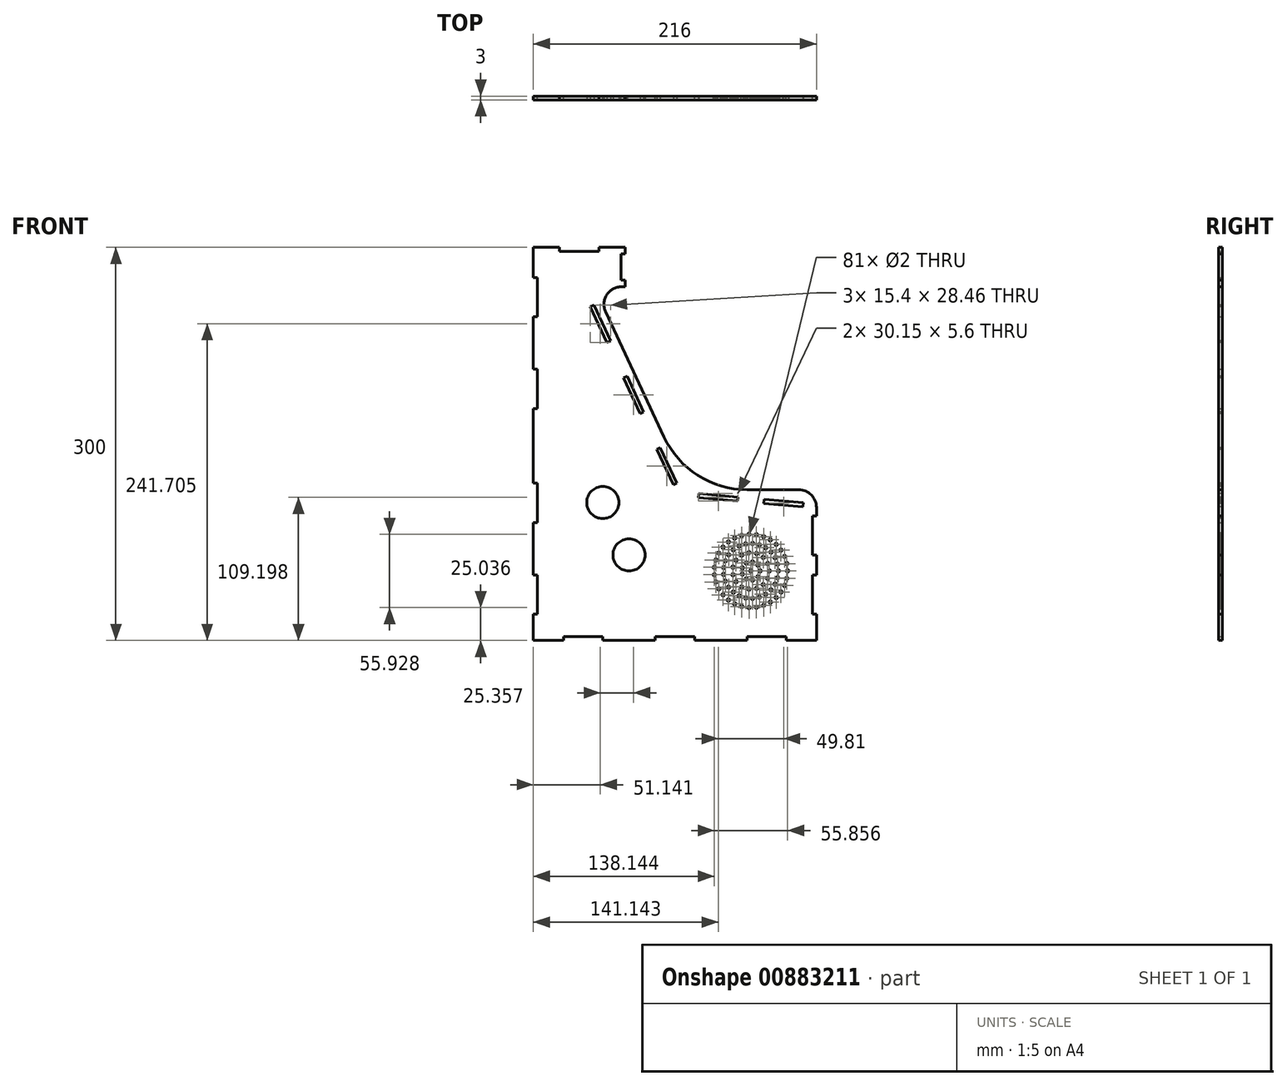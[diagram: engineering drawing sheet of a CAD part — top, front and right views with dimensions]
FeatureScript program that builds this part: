
annotation { "Feature Type Name" : "Feature", "Feature Type Description" : "" }
export const myFeature = defineFeature(function(context is Context, id is Id, definition is map)
    precondition{}
    {
        {
            var Q0;
            Q0=qCreatedBy(makeId("Front.planeOp"),FACE);
            var sketch = newSketch(context, id + "F0", { "sketchPlane" : qUnion([Q0])});
            skLineSegment(sketch, "E0", {"start": v(0, 0) * mm, "end": v(216, 0) * mm});
            skLineSegment(sketch, "E1", {"start": v(216, 0) * mm, "end": v(216, 115) * mm});
            skLineSegment(sketch, "E2", {"start": v(216, 115) * mm, "end": v(118.5, 115) * mm});
            skLineSegment(sketch, "E3", {"start": v(118.5, 115) * mm, "end": v(46.22, 270) * mm});
            skLineSegment(sketch, "E4", {"start": v(46.22, 270) * mm, "end": v(70, 270) * mm});
            skLineSegment(sketch, "E5", {"start": v(70, 270) * mm, "end": v(70, 300) * mm});
            skLineSegment(sketch, "E6", {"start": v(70, 300) * mm, "end": v(0, 300) * mm});
            skLineSegment(sketch, "E7", {"start": v(0, 300) * mm, "end": v(0, 0) * mm});
            skLineSegment(sketch, "E8", {"start": v(0, 277) * mm, "end": v(3, 277) * mm});
            skLineSegment(sketch, "E9", {"start": v(3, 277) * mm, "end": v(3, 247) * mm});
            skLineSegment(sketch, "E10", {"start": v(3, 247) * mm, "end": v(0, 247) * mm});
            skLineSegment(sketch, "E11", {"start": v(0, 207) * mm, "end": v(3, 207) * mm});
            skLineSegment(sketch, "E12", {"start": v(3, 207) * mm, "end": v(3, 177) * mm});
            skLineSegment(sketch, "E13", {"start": v(3, 177) * mm, "end": v(0, 177) * mm});
            skLineSegment(sketch, "E14", {"start": v(0, 120) * mm, "end": v(3, 120) * mm});
            skLineSegment(sketch, "E15", {"start": v(3, 120) * mm, "end": v(3, 90) * mm});
            skLineSegment(sketch, "E16", {"start": v(3, 90) * mm, "end": v(0, 90) * mm});
            skLineSegment(sketch, "E17", {"start": v(0, 50) * mm, "end": v(3, 50) * mm});
            skLineSegment(sketch, "E18", {"start": v(3, 50) * mm, "end": v(3, 20) * mm});
            skLineSegment(sketch, "E19", {"start": v(3, 20) * mm, "end": v(0, 20) * mm});
            skLineSegment(sketch, "E20", {"start": v(23, 0) * mm, "end": v(23, 3) * mm});
            skLineSegment(sketch, "E21", {"start": v(23, 3) * mm, "end": v(53, 3) * mm});
            skLineSegment(sketch, "E22", {"start": v(53, 3) * mm, "end": v(53, 0) * mm});
            skLineSegment(sketch, "E23", {"start": v(93, 0) * mm, "end": v(93, 3) * mm});
            skLineSegment(sketch, "E24", {"start": v(93, 3) * mm, "end": v(123, 3) * mm});
            skLineSegment(sketch, "E25", {"start": v(123, 3) * mm, "end": v(123, 0) * mm});
            skLineSegment(sketch, "E26", {"start": v(163, 0) * mm, "end": v(163, 3) * mm});
            skLineSegment(sketch, "E27", {"start": v(163, 3) * mm, "end": v(193, 3) * mm});
            skLineSegment(sketch, "E28", {"start": v(193, 3) * mm, "end": v(193, 0) * mm});
            skLineSegment(sketch, "E29", {"start": v(216, 20) * mm, "end": v(213, 20) * mm});
            skLineSegment(sketch, "E30", {"start": v(213, 20) * mm, "end": v(213, 50) * mm});
            skLineSegment(sketch, "E31", {"start": v(213, 50) * mm, "end": v(216, 50) * mm});
            skLineSegment(sketch, "E32", {"start": v(216, 65) * mm, "end": v(213, 65) * mm});
            skLineSegment(sketch, "E33", {"start": v(213, 65) * mm, "end": v(213, 95) * mm});
            skLineSegment(sketch, "E34", {"start": v(213, 95) * mm, "end": v(216, 95) * mm});
            skLineSegment(sketch, "E35", {"start": v(20, 300) * mm, "end": v(20, 297) * mm});
            skLineSegment(sketch, "E36", {"start": v(20, 297) * mm, "end": v(50, 297) * mm});
            skLineSegment(sketch, "E37", {"start": v(50, 297) * mm, "end": v(50, 300) * mm});
            skLineSegment(sketch, "E38", {"start": v(70, 295) * mm, "end": v(67, 295) * mm});
            skLineSegment(sketch, "E39", {"start": v(67, 295) * mm, "end": v(67, 275) * mm});
            skLineSegment(sketch, "E40", {"start": v(67, 275) * mm, "end": v(70, 275) * mm});
            skPoint(sketch, "E41", {"position": v(108, 3) * mm});
            skPoint(sketch, "E42", {"position": v(108, 0) * mm});
            skPoint(sketch, "E43", {"position": v(167.25, 115) * mm});
            skSolve(sketch);
        }
        {
            var Q0;
            {var subQ12=sQuery(id+"F0.wireOp",EDGE,"E2");Q0=makeQuery(id+"F0.imprint","IMPRINT",FACE,{"disambiguationData":[TD([[makeQuery(id+"F0.imprint","IMPRINT",EDGE,{"derivedFrom":subQ12}),1.0]])]});}
            var Q1;
            {var subQ0=sQuery(id+"F0.wireOp",EDGE,"E4");Q1=makeQuery(id+"F0.imprint","IMPRINT",FACE,{"disambiguationData":[TD([[makeQuery(id+"F0.imprint","IMPRINT",EDGE,{"derivedFrom":subQ0}),-1.0]])]});}
            var Q2;
            {var subQ3=sQuery(id+"F0.wireOp",EDGE,"8a221613-648f-4b06-892d-30c6be6bba23");Q2=makeQuery(id+"F0.imprint","IMPRINT",FACE,{"disambiguationData":[TD([[makeQuery(id+"F0.imprint","IMPRINT",EDGE,{"derivedFrom":subQ3}),-1.0]])]});}
            var Q3;
            {var subQ3=sQuery(id+"F0.wireOp",EDGE,"1dd4d70c-26e7-4ac6-b2af-ccda843abb65");Q3=makeQuery(id+"F0.imprint","IMPRINT",FACE,{"disambiguationData":[TD([[makeQuery(id+"F0.imprint","IMPRINT",EDGE,{"derivedFrom":subQ3}),1.0]])]});}
            extrude(context, id + "F1", {"entities" : qUnion([Q0, Q1, Q2, Q3]), "depth" : 3 * mm, "offsetDistance" : 25 * mm});
        }
        {
            var Q0;
            Q0=makeQuery(id+"F1.opExtrude","CAP_FACE",FACE,{"disambiguationData":[OSD([sQuery(id+"F0.wireOp",EDGE,"E0"),sQuery(id+"F0.wireOp",EDGE,"E1"),sQuery(id+"F0.wireOp",EDGE,"E2"),sQuery(id+"F0.wireOp",EDGE,"E3"),sQuery(id+"F0.wireOp",EDGE,"E4"),sQuery(id+"F0.wireOp",EDGE,"E5"),sQuery(id+"F0.wireOp",EDGE,"E6"),sQuery(id+"F0.wireOp",EDGE,"E7"),sQuery(id+"F0.wireOp",EDGE,"E8"),sQuery(id+"F0.wireOp",EDGE,"E9"),sQuery(id+"F0.wireOp",EDGE,"E10"),sQuery(id+"F0.wireOp",EDGE,"E11"),sQuery(id+"F0.wireOp",EDGE,"E12"),sQuery(id+"F0.wireOp",EDGE,"E13"),sQuery(id+"F0.wireOp",EDGE,"E14"),sQuery(id+"F0.wireOp",EDGE,"E15"),sQuery(id+"F0.wireOp",EDGE,"E16"),sQuery(id+"F0.wireOp",EDGE,"E17"),sQuery(id+"F0.wireOp",EDGE,"E18"),sQuery(id+"F0.wireOp",EDGE,"E19"),sQuery(id+"F0.wireOp",EDGE,"E20"),sQuery(id+"F0.wireOp",EDGE,"E21"),sQuery(id+"F0.wireOp",EDGE,"E22"),sQuery(id+"F0.wireOp",EDGE,"E23"),sQuery(id+"F0.wireOp",EDGE,"E24"),sQuery(id+"F0.wireOp",EDGE,"E25"),sQuery(id+"F0.wireOp",EDGE,"E26"),sQuery(id+"F0.wireOp",EDGE,"E27"),sQuery(id+"F0.wireOp",EDGE,"E28"),sQuery(id+"F0.wireOp",EDGE,"E29"),sQuery(id+"F0.wireOp",EDGE,"E30"),sQuery(id+"F0.wireOp",EDGE,"E31"),sQuery(id+"F0.wireOp",EDGE,"E32"),sQuery(id+"F0.wireOp",EDGE,"E33"),sQuery(id+"F0.wireOp",EDGE,"E34"),sQuery(id+"F0.wireOp",EDGE,"E35"),sQuery(id+"F0.wireOp",EDGE,"E36"),sQuery(id+"F0.wireOp",EDGE,"E37"),sQuery(id+"F0.wireOp",EDGE,"E38"),sQuery(id+"F0.wireOp",EDGE,"E39"),sQuery(id+"F0.wireOp",EDGE,"E40")])],"isStart":false});
            var sketch = newSketch(context, id + "F2", { "sketchPlane" : qUnion([Q0])});
            skLineSegment(sketch, "E44", {"start": v(0, 354.93) * mm, "end": v(177.98, -26.76) * mm, "construction": true});
            skLineSegment(sketch, "E45", {"start": v(3, 122.8) * mm, "end": v(213, 104.42) * mm, "construction": true});
            skLineSegment(sketch, "E46", {"start": v(126.33, 112) * mm, "end": v(156.22, 109.39) * mm});
            skLineSegment(sketch, "E47", {"start": v(156.22, 109.39) * mm, "end": v(155.96, 106.4) * mm});
            skLineSegment(sketch, "E48", {"start": v(155.96, 106.4) * mm, "end": v(126.07, 109.01) * mm});
            skLineSegment(sketch, "E49", {"start": v(126.07, 109.01) * mm, "end": v(126.33, 112) * mm});
            skLineSegment(sketch, "E50", {"start": v(176.14, 107.64) * mm, "end": v(175.88, 104.65) * mm});
            skLineSegment(sketch, "E51", {"start": v(175.88, 104.65) * mm, "end": v(205.77, 102.04) * mm});
            skLineSegment(sketch, "E52", {"start": v(205.77, 102.04) * mm, "end": v(206.03, 105.03) * mm});
            skLineSegment(sketch, "E53", {"start": v(206.03, 105.03) * mm, "end": v(176.14, 107.64) * mm});
            skLineSegment(sketch, "E54", {"start": v(71.52, 201.56) * mm, "end": v(68.8, 200.29) * mm});
            skLineSegment(sketch, "E55", {"start": v(68.8, 200.29) * mm, "end": v(81.48, 173.1) * mm});
            skLineSegment(sketch, "E56", {"start": v(81.48, 173.1) * mm, "end": v(84.2, 174.37) * mm});
            skLineSegment(sketch, "E57", {"start": v(84.2, 174.37) * mm, "end": v(71.52, 201.56) * mm});
            skLineSegment(sketch, "E58", {"start": v(96.88, 147.18) * mm, "end": v(94.16, 145.9) * mm});
            skLineSegment(sketch, "E59", {"start": v(94.16, 145.9) * mm, "end": v(106.83, 118.72) * mm});
            skLineSegment(sketch, "E60", {"start": v(106.83, 118.72) * mm, "end": v(109.55, 119.99) * mm});
            skLineSegment(sketch, "E61", {"start": v(109.55, 119.99) * mm, "end": v(96.88, 147.18) * mm});
            skPoint(sketch, "E62", {"position": v(112.72, 113.2) * mm});
            skLineSegment(sketch, "E63", {"start": v(58.84, 228.74) * mm, "end": v(46.16, 255.93) * mm});
            skLineSegment(sketch, "E64", {"start": v(46.16, 255.93) * mm, "end": v(43.44, 254.67) * mm});
            skLineSegment(sketch, "E65", {"start": v(43.44, 254.67) * mm, "end": v(56.12, 227.48) * mm});
            skLineSegment(sketch, "E66", {"start": v(56.12, 227.48) * mm, "end": v(58.84, 228.74) * mm});
            skCircle(sketch, "E67", {"center": v(73, 65.25) * mm, "radius": 12.25 * mm});
            skCircle(sketch, "E68", {"center": v(53, 105.25) * mm, "radius": 12.25 * mm});
            skSolve(sketch);
        }
        {
            var Q0;
            Q0 = qSketchRegion(id + "F2", true);
            var Q1;
            Q1=makeQuery(id+"F1.opExtrude","CAP_FACE",FACE,{"disambiguationData":[OSD([sQuery(id+"F0.wireOp",EDGE,"E0"),sQuery(id+"F0.wireOp",EDGE,"E1"),sQuery(id+"F0.wireOp",EDGE,"E2"),sQuery(id+"F0.wireOp",EDGE,"E3"),sQuery(id+"F0.wireOp",EDGE,"E4"),sQuery(id+"F0.wireOp",EDGE,"E5"),sQuery(id+"F0.wireOp",EDGE,"E6"),sQuery(id+"F0.wireOp",EDGE,"E7"),sQuery(id+"F0.wireOp",EDGE,"E8"),sQuery(id+"F0.wireOp",EDGE,"E9"),sQuery(id+"F0.wireOp",EDGE,"E10"),sQuery(id+"F0.wireOp",EDGE,"E11"),sQuery(id+"F0.wireOp",EDGE,"E12"),sQuery(id+"F0.wireOp",EDGE,"E13"),sQuery(id+"F0.wireOp",EDGE,"E14"),sQuery(id+"F0.wireOp",EDGE,"E15"),sQuery(id+"F0.wireOp",EDGE,"E16"),sQuery(id+"F0.wireOp",EDGE,"E17"),sQuery(id+"F0.wireOp",EDGE,"E18"),sQuery(id+"F0.wireOp",EDGE,"E19"),sQuery(id+"F0.wireOp",EDGE,"E20"),sQuery(id+"F0.wireOp",EDGE,"E21"),sQuery(id+"F0.wireOp",EDGE,"E22"),sQuery(id+"F0.wireOp",EDGE,"E23"),sQuery(id+"F0.wireOp",EDGE,"E24"),sQuery(id+"F0.wireOp",EDGE,"E25"),sQuery(id+"F0.wireOp",EDGE,"E26"),sQuery(id+"F0.wireOp",EDGE,"E27"),sQuery(id+"F0.wireOp",EDGE,"E28"),sQuery(id+"F0.wireOp",EDGE,"E29"),sQuery(id+"F0.wireOp",EDGE,"E30"),sQuery(id+"F0.wireOp",EDGE,"E31"),sQuery(id+"F0.wireOp",EDGE,"E32"),sQuery(id+"F0.wireOp",EDGE,"E33"),sQuery(id+"F0.wireOp",EDGE,"E34"),sQuery(id+"F0.wireOp",EDGE,"E35"),sQuery(id+"F0.wireOp",EDGE,"E36"),sQuery(id+"F0.wireOp",EDGE,"E37"),sQuery(id+"F0.wireOp",EDGE,"E38"),sQuery(id+"F0.wireOp",EDGE,"E39"),sQuery(id+"F0.wireOp",EDGE,"E40")])],"isStart":true});
            extrude(context, id + "F3", {"entities" : qUnion([Q0]), "operationType" : NewBodyOperationType.REMOVE, "endBound" : BoundingType.UP_TO_SURFACE, "oppositeDirection" : true, "depth" : 25 * mm, "endBoundEntityFace" : qUnion([Q1]), "offsetDistance" : 25 * mm});
        }
        {
            var Q0;
            Q0=makeQuery(id+"F1.opExtrude","SWEPT_EDGE",EDGE,{"disambiguationData":[OSD([sQuery(id+"F0.wireOp",EDGE,"E1"),sQuery(id+"F0.wireOp",EDGE,"E2")])]});
            var Q1;
            Q1=makeQuery(id+"F1.opExtrude","SWEPT_EDGE",EDGE,{"disambiguationData":[OSD([sQuery(id+"F0.wireOp",EDGE,"E3"),sQuery(id+"F0.wireOp",EDGE,"E4")])]});
            fillet(context, id + "F4", {"entities" : qUnion([Q0, Q1]), "radius" : 13.5 * mm, "tangentPropagation" : true, "allowEdgeOverflow" : false});
        }
        {
            var Q0;
            Q0=makeQuery(id+"F1.opExtrude","SWEPT_EDGE",EDGE,{"disambiguationData":[OSD([sQuery(id+"F0.wireOp",EDGE,"E2"),sQuery(id+"F0.wireOp",EDGE,"E3")])]});
            fillet(context, id + "F5", {"entities" : qUnion([Q0]), "radius" : 70 * mm, "tangentPropagation" : true, "allowEdgeOverflow" : false});
        }
        {
            var Q0;
            Q0=makeQuery(id+"F1.opExtrude","CAP_FACE",FACE,{"disambiguationData":[OSD([sQuery(id+"F0.wireOp",EDGE,"E0"),sQuery(id+"F0.wireOp",EDGE,"E1"),sQuery(id+"F0.wireOp",EDGE,"E2"),sQuery(id+"F0.wireOp",EDGE,"E3"),sQuery(id+"F0.wireOp",EDGE,"E4"),sQuery(id+"F0.wireOp",EDGE,"E5"),sQuery(id+"F0.wireOp",EDGE,"E6"),sQuery(id+"F0.wireOp",EDGE,"E7"),sQuery(id+"F0.wireOp",EDGE,"E8"),sQuery(id+"F0.wireOp",EDGE,"E9"),sQuery(id+"F0.wireOp",EDGE,"E10"),sQuery(id+"F0.wireOp",EDGE,"E11"),sQuery(id+"F0.wireOp",EDGE,"E12"),sQuery(id+"F0.wireOp",EDGE,"E13"),sQuery(id+"F0.wireOp",EDGE,"E14"),sQuery(id+"F0.wireOp",EDGE,"E15"),sQuery(id+"F0.wireOp",EDGE,"E16"),sQuery(id+"F0.wireOp",EDGE,"E17"),sQuery(id+"F0.wireOp",EDGE,"E18"),sQuery(id+"F0.wireOp",EDGE,"E19"),sQuery(id+"F0.wireOp",EDGE,"E20"),sQuery(id+"F0.wireOp",EDGE,"E21"),sQuery(id+"F0.wireOp",EDGE,"E22"),sQuery(id+"F0.wireOp",EDGE,"E23"),sQuery(id+"F0.wireOp",EDGE,"E24"),sQuery(id+"F0.wireOp",EDGE,"E25"),sQuery(id+"F0.wireOp",EDGE,"E26"),sQuery(id+"F0.wireOp",EDGE,"E27"),sQuery(id+"F0.wireOp",EDGE,"E28"),sQuery(id+"F0.wireOp",EDGE,"E29"),sQuery(id+"F0.wireOp",EDGE,"E30"),sQuery(id+"F0.wireOp",EDGE,"E31"),sQuery(id+"F0.wireOp",EDGE,"E32"),sQuery(id+"F0.wireOp",EDGE,"E33"),sQuery(id+"F0.wireOp",EDGE,"E34"),sQuery(id+"F0.wireOp",EDGE,"E35"),sQuery(id+"F0.wireOp",EDGE,"E36"),sQuery(id+"F0.wireOp",EDGE,"E37"),sQuery(id+"F0.wireOp",EDGE,"E38"),sQuery(id+"F0.wireOp",EDGE,"E39"),sQuery(id+"F0.wireOp",EDGE,"E40")])],"isStart":false});
            var sketch = newSketch(context, id + "F6", { "sketchPlane" : qUnion([Q0])});
            skCircle(sketch, "E69", {"center": v(166, 53) * mm, "radius": 1 * mm});
            skCircle(sketch, "E70", {"center": v(173, 53) * mm, "radius": 1 * mm});
            skCircle(sketch, "E71", {"center": v(180, 53) * mm, "radius": 1 * mm});
            skCircle(sketch, "E72", {"center": v(187, 53) * mm, "radius": 1 * mm});
            skCircle(sketch, "E73.1.0", {"center": v(171.36, 57.5) * mm, "radius": 1 * mm});
            skCircle(sketch, "E73.2.0", {"center": v(167.22, 59.9) * mm, "radius": 1 * mm});
            skCircle(sketch, "E73.3.0", {"center": v(162.5, 59.06) * mm, "radius": 1 * mm});
            skCircle(sketch, "E73.4.0", {"center": v(159.42, 55.4) * mm, "radius": 1 * mm});
            skCircle(sketch, "E73.5.0", {"center": v(159.42, 50.6) * mm, "radius": 1 * mm});
            skCircle(sketch, "E73.6.0", {"center": v(162.5, 46.94) * mm, "radius": 1 * mm});
            skCircle(sketch, "E73.7.0", {"center": v(167.22, 46.1) * mm, "radius": 1 * mm});
            skCircle(sketch, "E74.1.0", {"center": v(178.79, 58.7) * mm, "radius": 1 * mm});
            skCircle(sketch, "E74.2.0", {"center": v(175.37, 63.4) * mm, "radius": 1 * mm});
            skCircle(sketch, "E74.3.0", {"center": v(170.33, 66.31) * mm, "radius": 1 * mm});
            skCircle(sketch, "E74.4.0", {"center": v(164.54, 66.92) * mm, "radius": 1 * mm});
            skCircle(sketch, "E74.5.0", {"center": v(159, 65.12) * mm, "radius": 1 * mm});
            skCircle(sketch, "E74.6.0", {"center": v(154.67, 61.23) * mm, "radius": 1 * mm});
            skCircle(sketch, "E74.7.0", {"center": v(152.3, 55.91) * mm, "radius": 1 * mm});
            skCircle(sketch, "E74.8.0", {"center": v(152.3, 50.09) * mm, "radius": 1 * mm});
            skCircle(sketch, "E74.9.0", {"center": v(154.67, 44.77) * mm, "radius": 1 * mm});
            skCircle(sketch, "E74.10.0", {"center": v(159, 40.88) * mm, "radius": 1 * mm});
            skCircle(sketch, "E74.11.0", {"center": v(164.54, 39.08) * mm, "radius": 1 * mm});
            skCircle(sketch, "E74.12.0", {"center": v(170.33, 39.69) * mm, "radius": 1 * mm});
            skCircle(sketch, "E74.13.0", {"center": v(175.37, 42.6) * mm, "radius": 1 * mm});
            skCircle(sketch, "E74.14.0", {"center": v(178.79, 47.3) * mm, "radius": 1 * mm});
            skCircle(sketch, "E75.1.0", {"center": v(186.34, 58.22) * mm, "radius": 1 * mm});
            skCircle(sketch, "E75.2.0", {"center": v(184.4, 63.12) * mm, "radius": 1 * mm});
            skCircle(sketch, "E75.3.0", {"center": v(181.3, 67.38) * mm, "radius": 1 * mm});
            skCircle(sketch, "E75.4.0", {"center": v(177.25, 70.73) * mm, "radius": 1 * mm});
            skCircle(sketch, "E75.5.0", {"center": v(172.49, 72.97) * mm, "radius": 1 * mm});
            skCircle(sketch, "E75.6.0", {"center": v(167.32, 73.96) * mm, "radius": 1 * mm});
            skCircle(sketch, "E75.7.0", {"center": v(162.06, 73.63) * mm, "radius": 1 * mm});
            skCircle(sketch, "E75.8.0", {"center": v(157.06, 72) * mm, "radius": 1 * mm});
            skCircle(sketch, "E75.9.0", {"center": v(152.61, 69.18) * mm, "radius": 1 * mm});
            skCircle(sketch, "E75.10.0", {"center": v(149.01, 65.34) * mm, "radius": 1 * mm});
            skCircle(sketch, "E75.11.0", {"center": v(146.47, 60.73) * mm, "radius": 1 * mm});
            skCircle(sketch, "E75.12.0", {"center": v(145.17, 55.63) * mm, "radius": 1 * mm});
            skCircle(sketch, "E75.13.0", {"center": v(145.17, 50.37) * mm, "radius": 1 * mm});
            skCircle(sketch, "E75.14.0", {"center": v(146.47, 45.27) * mm, "radius": 1 * mm});
            skCircle(sketch, "E75.15.0", {"center": v(149.01, 40.66) * mm, "radius": 1 * mm});
            skCircle(sketch, "E75.16.0", {"center": v(152.61, 36.82) * mm, "radius": 1 * mm});
            skCircle(sketch, "E75.17.0", {"center": v(157.06, 34) * mm, "radius": 1 * mm});
            skCircle(sketch, "E75.18.0", {"center": v(162.06, 32.37) * mm, "radius": 1 * mm});
            skCircle(sketch, "E75.19.0", {"center": v(167.32, 32.04) * mm, "radius": 1 * mm});
            skCircle(sketch, "E75.20.0", {"center": v(172.49, 33.03) * mm, "radius": 1 * mm});
            skCircle(sketch, "E75.21.0", {"center": v(177.25, 35.27) * mm, "radius": 1 * mm});
            skCircle(sketch, "E75.22.0", {"center": v(181.3, 38.62) * mm, "radius": 1 * mm});
            skCircle(sketch, "E75.23.0", {"center": v(184.4, 42.88) * mm, "radius": 1 * mm});
            skCircle(sketch, "E75.24.0", {"center": v(186.34, 47.78) * mm, "radius": 1 * mm});
            skCircle(sketch, "E76", {"center": v(194, 53) * mm, "radius": 1 * mm});
            skCircle(sketch, "E77.1.0", {"center": v(193.43, 58.64) * mm, "radius": 1 * mm});
            skCircle(sketch, "E77.2.0", {"center": v(191.73, 64.04) * mm, "radius": 1 * mm});
            skCircle(sketch, "E77.3.0", {"center": v(188.98, 69) * mm, "radius": 1 * mm});
            skCircle(sketch, "E77.4.0", {"center": v(185.3, 73.3) * mm, "radius": 1 * mm});
            skCircle(sketch, "E77.5.0", {"center": v(180.81, 76.76) * mm, "radius": 1 * mm});
            skCircle(sketch, "E77.6.0", {"center": v(175.72, 79.26) * mm, "radius": 1 * mm});
            skCircle(sketch, "E77.7.0", {"center": v(170.24, 80.68) * mm, "radius": 1 * mm});
            skCircle(sketch, "E77.8.0", {"center": v(164.58, 80.96) * mm, "radius": 1 * mm});
            skCircle(sketch, "E77.9.0", {"center": v(158.98, 80.1) * mm, "radius": 1 * mm});
            skCircle(sketch, "E77.10.0", {"center": v(153.67, 78.14) * mm, "radius": 1 * mm});
            skCircle(sketch, "E77.11.0", {"center": v(148.86, 75.14) * mm, "radius": 1 * mm});
            skCircle(sketch, "E77.12.0", {"center": v(144.75, 71.24) * mm, "radius": 1 * mm});
            skCircle(sketch, "E77.13.0", {"center": v(141.52, 66.59) * mm, "radius": 1 * mm});
            skCircle(sketch, "E77.14.0", {"center": v(139.28, 61.38) * mm, "radius": 1 * mm});
            skCircle(sketch, "E77.15.0", {"center": v(138.14, 55.83) * mm, "radius": 1 * mm});
            skCircle(sketch, "E77.16.0", {"center": v(138.14, 50.17) * mm, "radius": 1 * mm});
            skCircle(sketch, "E77.17.0", {"center": v(139.28, 44.62) * mm, "radius": 1 * mm});
            skCircle(sketch, "E77.18.0", {"center": v(141.52, 39.41) * mm, "radius": 1 * mm});
            skCircle(sketch, "E77.19.0", {"center": v(144.75, 34.76) * mm, "radius": 1 * mm});
            skCircle(sketch, "E77.20.0", {"center": v(148.86, 30.86) * mm, "radius": 1 * mm});
            skCircle(sketch, "E77.21.0", {"center": v(153.67, 27.86) * mm, "radius": 1 * mm});
            skCircle(sketch, "E77.22.0", {"center": v(158.98, 25.9) * mm, "radius": 1 * mm});
            skCircle(sketch, "E77.23.0", {"center": v(164.58, 25.04) * mm, "radius": 1 * mm});
            skCircle(sketch, "E77.24.0", {"center": v(170.24, 25.32) * mm, "radius": 1 * mm});
            skCircle(sketch, "E77.25.0", {"center": v(175.72, 26.74) * mm, "radius": 1 * mm});
            skCircle(sketch, "E77.26.0", {"center": v(180.81, 29.24) * mm, "radius": 1 * mm});
            skCircle(sketch, "E77.27.0", {"center": v(185.3, 32.7) * mm, "radius": 1 * mm});
            skCircle(sketch, "E77.28.0", {"center": v(188.98, 37) * mm, "radius": 1 * mm});
            skCircle(sketch, "E77.29.0", {"center": v(191.73, 41.96) * mm, "radius": 1 * mm});
            skCircle(sketch, "E77.30.0", {"center": v(193.43, 47.36) * mm, "radius": 1 * mm});
            skCircle(sketch, "E78.1.8.0", {"center": v(171.36, 48.5) * mm, "radius": 1 * mm});
            skSolve(sketch);
        }
        {
            var Q0;
            Q0 = qSketchRegion(id + "F6", true);
            var Q1;
            Q1=makeQuery(id+"F1.opExtrude","CAP_FACE",FACE,{"disambiguationData":[OSD([sQuery(id+"F0.wireOp",EDGE,"E0"),sQuery(id+"F0.wireOp",EDGE,"E1"),sQuery(id+"F0.wireOp",EDGE,"E2"),sQuery(id+"F0.wireOp",EDGE,"E3"),sQuery(id+"F0.wireOp",EDGE,"E4"),sQuery(id+"F0.wireOp",EDGE,"E5"),sQuery(id+"F0.wireOp",EDGE,"E6"),sQuery(id+"F0.wireOp",EDGE,"E7"),sQuery(id+"F0.wireOp",EDGE,"E8"),sQuery(id+"F0.wireOp",EDGE,"E9"),sQuery(id+"F0.wireOp",EDGE,"E10"),sQuery(id+"F0.wireOp",EDGE,"E11"),sQuery(id+"F0.wireOp",EDGE,"E12"),sQuery(id+"F0.wireOp",EDGE,"E13"),sQuery(id+"F0.wireOp",EDGE,"E14"),sQuery(id+"F0.wireOp",EDGE,"E15"),sQuery(id+"F0.wireOp",EDGE,"E16"),sQuery(id+"F0.wireOp",EDGE,"E17"),sQuery(id+"F0.wireOp",EDGE,"E18"),sQuery(id+"F0.wireOp",EDGE,"E19"),sQuery(id+"F0.wireOp",EDGE,"E20"),sQuery(id+"F0.wireOp",EDGE,"E21"),sQuery(id+"F0.wireOp",EDGE,"E22"),sQuery(id+"F0.wireOp",EDGE,"E23"),sQuery(id+"F0.wireOp",EDGE,"E24"),sQuery(id+"F0.wireOp",EDGE,"E25"),sQuery(id+"F0.wireOp",EDGE,"E26"),sQuery(id+"F0.wireOp",EDGE,"E27"),sQuery(id+"F0.wireOp",EDGE,"E28"),sQuery(id+"F0.wireOp",EDGE,"E29"),sQuery(id+"F0.wireOp",EDGE,"E30"),sQuery(id+"F0.wireOp",EDGE,"E31"),sQuery(id+"F0.wireOp",EDGE,"E32"),sQuery(id+"F0.wireOp",EDGE,"E33"),sQuery(id+"F0.wireOp",EDGE,"E34"),sQuery(id+"F0.wireOp",EDGE,"E35"),sQuery(id+"F0.wireOp",EDGE,"E36"),sQuery(id+"F0.wireOp",EDGE,"E37"),sQuery(id+"F0.wireOp",EDGE,"E38"),sQuery(id+"F0.wireOp",EDGE,"E39"),sQuery(id+"F0.wireOp",EDGE,"E40")])],"isStart":true});
            extrude(context, id + "F7", {"entities" : qUnion([Q0]), "operationType" : NewBodyOperationType.REMOVE, "endBound" : BoundingType.UP_TO_SURFACE, "oppositeDirection" : true, "depth" : 25 * mm, "endBoundEntityFace" : qUnion([Q1]), "offsetDistance" : 25 * mm});
        }
    });
